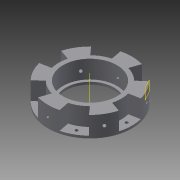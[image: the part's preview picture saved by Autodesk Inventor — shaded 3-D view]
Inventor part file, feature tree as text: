
AUTODESK INVENTOR PART (.ipt)
format: ipt  version: 2015 (Build 190159000, 159)  size: 209,920 bytes
history: native  units: in
note: dims shown in document units (in); Inventor stores cm internally (conversion verified against a paired STEP export)
features: sketch x7, extrude x4, hole x4, pattern_circular x4, plane x2
ambient origin geometry x8: Origin, YZ Plane, XZ Plane, XY Plane, X Axis, Y Axis, Z Axis, Center Point
bodies: Solid1 (feature_tree)
feature tree (21):
  extrude  "Extrusion1"  Depth=7.0in
  extrude  "Extrusion4"  Depth=5.21in
  hole  "Hole4"  [1 undecoded]
  pattern_circular  "Circular Pattern4"  Count=6 Angle=360.0deg
  extrude  "Extrusion5"  Depth=4.5in
  plane  "Work Plane4"
  hole  "Hole5"  [1 undecoded]
  pattern_circular  "Circular Pattern5"  [2 undecoded]
  hole  "Hole1"  [1 undecoded]
  pattern_circular  "Circular Pattern1"  [2 undecoded]
  extrude  "Extrusion3"  Depth=0.25in
  plane  "Work Plane3"
  hole  "Hole3"  [1 undecoded]
  pattern_circular  "Circular Pattern3"  Angle=30.0deg  [1 undecoded]
  sketch  "Sketch1"  dims[d0=4.026in d1=7.0in]
  sketch  "Sketch2"  dims[d2=0.2in d3=0.0in d4=5.21in]
  sketch  "Sketch4"  dims[d12=0.25in d13=0.75in d14=0.375in d15=0.25in d16=0.5635in d17=1.0in d18=0.8108in d19=2.3622in d20=360.0deg]
  sketch  "Sketch6"  dims[d22=1.51in d23=0.0in]
  sketch  "Sketch9"  dims[d35=0.855in]
  sketch  "Sketch11"  dims[d36=0.25in]
  sketch  "Sketch12"  dims[d37=0.25in d38=0.75in d39=0.375in d40=0.25in d41=0.5635in d42=1.5425in d43=0.8108in d44=2.3622in d45=360.0deg d47=4.5in d48=1.5in d49=0.0in d50=0.895in d51=0.25in d52=0.895in d54=0.25in d55=0.25in d56=0.75in d57=0.375in d58=0.25in d59=0.5635in d60=1.0in d61=0.8108in d62=2.3622in d63=360.0deg d71=30.0deg d72=1.5in d73=0.0in d74=0.85in d75=0.25in d76=0.25in d77=0.75in d78=0.375in d79=0.25in d80=0.5635in d81=2.0in d82=0.0in d83=2.3622in d84=360.0deg]
note: 9 required parameter values undecoded (feature->parameter linkage not recoverable at this tier; creation-order binding heuristic only, values carry confidence <= 0.55)
